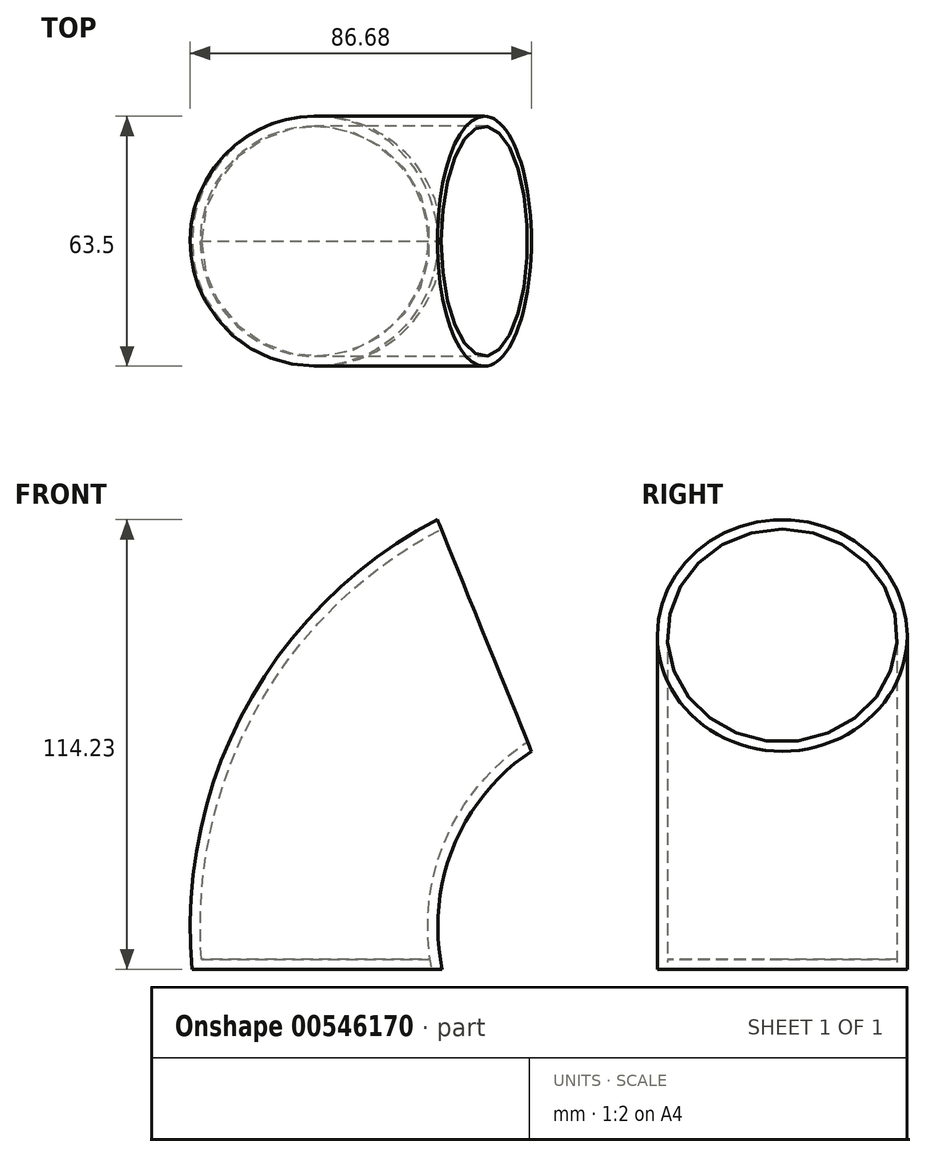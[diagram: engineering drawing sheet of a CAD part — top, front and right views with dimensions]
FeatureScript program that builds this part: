
annotation { "Feature Type Name" : "Feature", "Feature Type Description" : "" }
export const myFeature = defineFeature(function(context is Context, id is Id, definition is map)
    precondition{}
    {
        {
            var Q0;
            Q0=qCreatedBy(makeId("Top.planeOp"),FACE);
            var sketch = newSketch(context, id + "F0", { "sketchPlane" : qUnion([Q0])});
            skCircle(sketch, "E0", {"center": v(0, 0) * mm, "radius": 31.75 * mm});
            skSolve(sketch);
        }
        {
            var Q0;
            Q0=qCreatedBy(makeId("Front.planeOp"),FACE);
            var sketch = newSketch(context, id + "F1", { "sketchPlane" : qUnion([Q0])});
            skArc(sketch, "E1", {"start": v(42.48, 84.8) * mm, "mid": v(8.3, 48.9) * mm, "end": v(0, 0) * mm});
            skSolve(sketch);
        }
        {
            var Q0;
            Q0=makeQuery(id+"F0.imprint","IMPRINT",FACE,{"disambiguationData":[TD([[makeQuery(id+"F0.imprint","IMPRINT",EDGE,{"derivedFrom":sQuery(id+"F0.wireOp",EDGE,"E0")}),1.0]])]});
            var Q1;
            Q1=sQuery(id+"F1.wireOp",EDGE,"E1");
            sweep(context, id + "F2", {"profiles" : qUnion([Q0]), "path" : qUnion([Q1])});
        }
        {
            var Q0;
            Q0=makeQuery(id+"F2.opSweep","CAP_FACE",FACE,{"disambiguationData":[OSD([sQuery(id+"F0.wireOp",EDGE,"E0"),sQuery(id+"F1.wireOp",VERTEX,"E1.start")])],"isStart":false});
            shell(context, id + "F3", {"entities" : qUnion([Q0]), "thickness" : 2.54 * mm});
        }
    });
